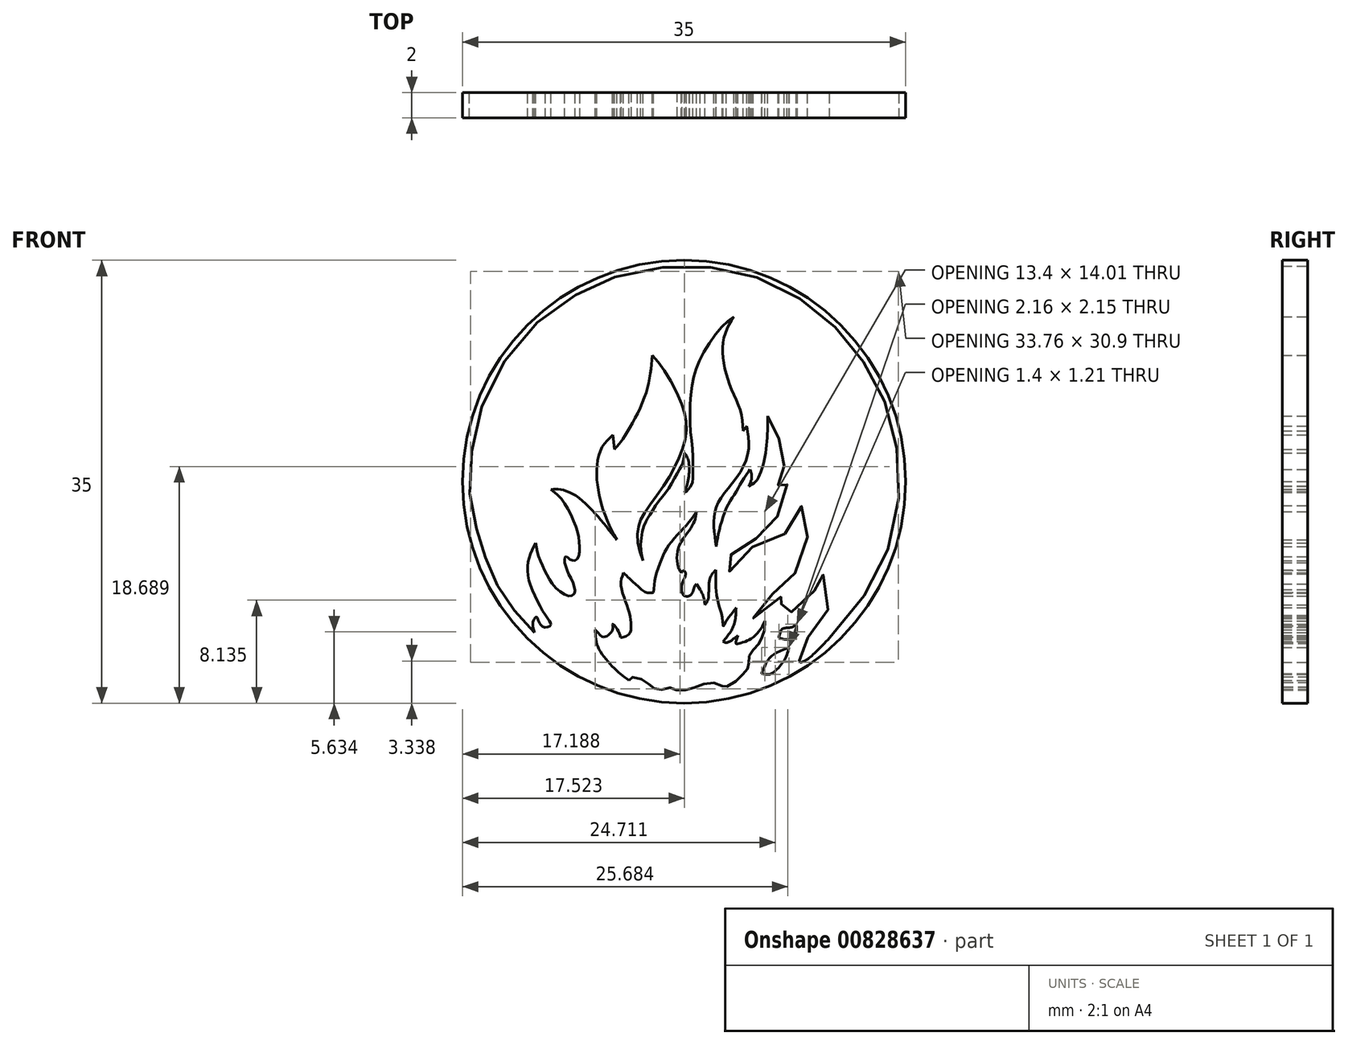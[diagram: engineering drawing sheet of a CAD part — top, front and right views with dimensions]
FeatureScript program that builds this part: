
annotation { "Feature Type Name" : "Feature", "Feature Type Description" : "" }
export const myFeature = defineFeature(function(context is Context, id is Id, definition is map)
    precondition{}
    {
        {
            var Q0;
            Q0=qCreatedBy(makeId("Front.planeOp"),FACE);
            var sketch = newSketch(context, id + "F0", { "sketchPlane" : qUnion([Q0])});
            skCircle(sketch, "E0", {"center": v(0, 0) * mm, "radius": 17.5 * mm});
            skSolve(sketch);
        }
        {
            var Q0;
            Q0=makeQuery(id+"F0.imprint","IMPRINT",FACE,{"disambiguationData":[TD([[makeQuery(id+"F0.imprint","IMPRINT",EDGE,{"derivedFrom":sQuery(id+"F0.wireOp",EDGE,"E0")}),1.0]])]});
            var sketch = newSketch(context, id + "F1", { "sketchPlane" : qUnion([Q0])});
            skFitSpline(sketch, "E1", {"points": [v(-11.8, -11.92) * mm, v(-12.84, -10.88) * mm, v(-13.93, -9.45) * mm, v(-14.73, -8.22) * mm, v(-15.3, -6.9) * mm, v(-16.04, -5.03) * mm, v(-16.38, -3.72) * mm, v(-16.87, -1.59) * mm, v(-16.87, 1.43) * mm, v(-16.3, 4.94) * mm, v(-14.52, 8.98) * mm, v(-11.7, 12.5) * mm, v(-8.56, 14.76) * mm, v(-5.54, 16.14) * mm, v(-1.46, 16.96) * mm, v(2.55, 16.9) * mm, v(6.38, 15.89) * mm, v(9.9, 13.94) * mm, v(12.54, 11.56) * mm, v(14.6, 8.73) * mm, v(16.18, 5.4) * mm, v(16.93, 1.26) * mm, v(16.68, -3.26) * mm, v(14.92, -7.9) * mm, v(11.97, -11.8) * mm, v(9.15, -14.25) * mm, v(9.08, -13.24) * mm, v(10.6, -11.48) * mm, v(11.47, -9.04) * mm, v(10.84, -7.22) * mm, v(10.53, -8.16) * mm, v(9.21, -9.66) * mm, v(7.9, -10.54) * mm, v(7.51, -10.04) * mm, v(8.33, -8.85) * mm, v(6.89, -9.6) * mm, v(5.44, -10.8) * mm, v(6.95, -8.91) * mm, v(8.52, -7.47) * mm, v(9.71, -5.14) * mm, v(9.34, -1.88) * mm, v(8.83, -3.2) * mm, v(6.45, -4.83) * mm, v(4.5, -5.77) * mm, v(3.37, -7.28) * mm, v(3.62, -5.9) * mm, v(5.05, -4.88) * mm, v(6.78, -3.54) * mm, v(7.8, -1.77) * mm, v(8.1, 0) * mm, v(7.85, -0.2) * mm, v(7.45, -0.33) * mm, v(7.63, 0.22) * mm, v(7.89, 1.19) * mm, v(7.8, 2.25) * mm, v(7.04, 4.54) * mm, v(6.6, 5.19) * mm], "startDerivative": vector(-72.23, 66.96) * mm, "endDerivative": vector(-39.78, 46.76) * mm});
            skFitSpline(sketch, "E2", {"points": [v(6.6, 5.19) * mm, v(6.47, 2.59) * mm, v(5.79, 0.19) * mm, v(5.1, -0.37) * mm], "startDerivative": vector(-0.04, -6.43) * mm, "endDerivative": vector(-3.2, -1.68) * mm});
            skFitSpline(sketch, "E3", {"points": [v(5.1, -0.37) * mm, v(5.34, 0.32) * mm, v(5.22, 0.96) * mm], "startDerivative": vector(0.66, 1.34) * mm, "endDerivative": vector(-0.43, 1.32) * mm});
            skFitSpline(sketch, "E4", {"points": [v(5.22, 0.96) * mm, v(4.8, 0.38) * mm, v(4.1, -0.8) * mm, v(3.33, -2.11) * mm, v(2.72, -4.1) * mm, v(2.55, -5.14) * mm], "startDerivative": vector(-2.74, -3.5) * mm, "endDerivative": vector(-0.66, -5.22) * mm});
            skFitSpline(sketch, "E5", {"points": [v(2.55, -5.14) * mm, v(2.36, -3.76) * mm, v(2.42, -2.43) * mm, v(3, -1.12) * mm, v(4.38, 0.67) * mm, v(5.1, 2.68) * mm, v(4.94, 4.4) * mm], "startDerivative": vector(-1.5, 9.13) * mm, "endDerivative": vector(-1.89, 10.06) * mm});
            skFitSpline(sketch, "E6", {"points": [v(4.94, 4.4) * mm, v(4.66, 4) * mm], "startDerivative": vector(-0.29, -0.4) * mm, "endDerivative": vector(-0.29, -0.4) * mm});
            skFitSpline(sketch, "E7", {"points": [v(4.66, 4) * mm, v(4.44, 5.6) * mm, v(3.76, 7.28) * mm, v(3.2, 9) * mm, v(3.03, 10.6) * mm, v(3.34, 11.94) * mm, v(3.94, 13.05) * mm], "startDerivative": vector(-0.6, 9.52) * mm, "endDerivative": vector(4.38, 7.18) * mm});
            skFitSpline(sketch, "E8", {"points": [v(3.94, 13.05) * mm, v(2.79, 12.03) * mm, v(1.39, 9.94) * mm, v(0.77, 8.34) * mm, v(0.5, 6.49) * mm, v(0.47, 4.47) * mm, v(0.64, 2.75) * mm, v(0.7, 1.38) * mm, v(0.7, 0.32) * mm, v(0.6, -0.24) * mm, v(0.19, -0.8) * mm], "startDerivative": vector(-10.97, -8.38) * mm, "endDerivative": vector(-6.85, -7.97) * mm});
            skFitSpline(sketch, "E9", {"points": [v(0.19, -0.8) * mm, v(0.03, -0.85) * mm], "startDerivative": vector(-0.16, -0.06) * mm, "endDerivative": vector(-0.16, -0.06) * mm});
            skFitSpline(sketch, "E10", {"points": [v(0.03, -0.85) * mm, v(0.35, 0.25) * mm, v(0.35, 1.63) * mm, v(0.03, 2.28) * mm], "startDerivative": vector(1.06, 2.97) * mm, "endDerivative": vector(-1.36, 2.03) * mm});
            skFitSpline(sketch, "E11", {"points": [v(0.03, 2.28) * mm, v(-0.09, 1.52) * mm, v(-0.53, 0.69) * mm, v(-1.28, -0.6) * mm, v(-2.04, -1.6) * mm, v(-2.75, -2.69) * mm, v(-3.1, -3.32) * mm, v(-3.43, -4.97) * mm, v(-3.24, -6.23) * mm], "startDerivative": vector(-0.5, -7.58) * mm, "endDerivative": vector(2.2, -8.87) * mm});
            skFitSpline(sketch, "E12", {"points": [v(-3.24, -6.23) * mm, v(-3.66, -4.78) * mm, v(-3.63, -3.66) * mm, v(-3.34, -2.84) * mm, v(-2.48, -1.52) * mm, v(-1.22, 0.31) * mm, v(-0.4, 1.93) * mm, v(0.14, 3.5) * mm, v(0.14, 4.9) * mm, v(-0.25, 6.28) * mm, v(-1.5, 8.71) * mm, v(-2.52, 9.98) * mm], "startDerivative": vector(-6, 16.73) * mm, "endDerivative": vector(-10.81, 11.9) * mm});
            skFitSpline(sketch, "E13", {"points": [v(-2.52, 9.98) * mm, v(-3.09, 6.76) * mm, v(-4.87, 3.35) * mm, v(-5.51, 2.55) * mm], "startDerivative": vector(-0.64, -8.17) * mm, "endDerivative": vector(-2.66, -2.94) * mm});
            skFitSpline(sketch, "E14", {"points": [v(-5.51, 2.55) * mm, v(-5.61, 3.68) * mm], "startDerivative": vector(-0.1, 1.14) * mm, "endDerivative": vector(-0.1, 1.14) * mm});
            skFitSpline(sketch, "E15", {"points": [v(-5.61, 3.68) * mm, v(-6.44, 2.78) * mm, v(-6.88, 1.23) * mm, v(-6.78, -0.6) * mm, v(-6.26, -2.62) * mm, v(-5.32, -4.6) * mm], "startDerivative": vector(-5.48, -4.78) * mm, "endDerivative": vector(4.62, -8.74) * mm});
            skFitSpline(sketch, "E16", {"points": [v(-5.32, -4.6) * mm, v(-6.78, -2.8) * mm, v(-8.52, -1.13) * mm, v(-9.78, -0.6) * mm, v(-10.52, -0.6) * mm], "startDerivative": vector(-4.68, 5.98) * mm, "endDerivative": vector(-4.16, -0.36) * mm});
            skFitSpline(sketch, "E17", {"points": [v(-10.52, -0.6) * mm, v(-9.6, -1.5) * mm, v(-8.58, -3.5) * mm, v(-8.26, -4.97) * mm, v(-8.4, -6.07) * mm, v(-8.78, -6.23) * mm, v(-9.08, -6.1) * mm, v(-9.27, -5.93) * mm, v(-9.4, -5.95) * mm, v(-9.44, -6.4) * mm], "startDerivative": vector(6.3, -4.93) * mm, "endDerivative": vector(0.24, -6.61) * mm});
            skFitSpline(sketch, "E18", {"points": [v(-9.44, -6.4) * mm, v(-9.17, -7.18) * mm, v(-8.69, -8.23) * mm, v(-8.68, -8.83) * mm, v(-9.09, -9.04) * mm, v(-10.21, -8.31) * mm, v(-10.95, -7.12) * mm, v(-11.49, -5.9) * mm, v(-11.73, -4.84) * mm], "startDerivative": vector(1.97, -6.5) * mm, "endDerivative": vector(-1.43, 8) * mm});
            skFitSpline(sketch, "E19", {"points": [v(-11.73, -4.84) * mm, v(-12.2, -5.9) * mm, v(-12.35, -7.26) * mm, v(-11.73, -9.11) * mm, v(-10.78, -10.8) * mm, v(-10.52, -11.2) * mm, v(-10.6, -11.42) * mm, v(-10.96, -11.51) * mm], "startDerivative": vector(-3.32, -6.5) * mm, "endDerivative": vector(-4.63, -0.5) * mm});
            skFitSpline(sketch, "E20", {"points": [v(-10.96, -11.51) * mm, v(-11.15, -11.46) * mm, v(-11.5, -11.02) * mm, v(-11.65, -10.7) * mm, v(-11.86, -10.92) * mm, v(-11.94, -11.4) * mm, v(-11.8, -11.92) * mm], "startDerivative": vector(-1.55, 0.12) * mm, "endDerivative": vector(0.9, -2.65) * mm});
            skFitSpline(sketch, "E21", {"points": [v(-7.01, -11.69) * mm, v(-6.83, -13) * mm, v(-5.61, -14.65) * mm, v(-4.37, -15.7) * mm], "startDerivative": vector(0.01, -4.3) * mm, "endDerivative": vector(3.7, -2.87) * mm});
            skFitSpline(sketch, "E22", {"points": [v(-4.37, -15.7) * mm, v(-4.23, -15.47) * mm, v(-3.51, -15.55) * mm, v(-2.83, -15.98) * mm, v(-2.38, -16.33) * mm, v(-1.83, -16.43) * mm, v(-1.1, -16.27) * mm, v(-0.66, -16.45) * mm, v(0.18, -16.46) * mm, v(1.08, -16.18) * mm, v(2.15, -15.88) * mm, v(2.98, -16.12) * mm, v(3.2, -16.23) * mm, v(3.99, -15.83) * mm, v(4.67, -15.19) * mm, v(5.04, -14.73) * mm, v(5.12, -14.4) * mm, v(5.12, -13.89) * mm, v(5.33, -13.42) * mm, v(5.84, -12.88) * mm, v(6.13, -12.35) * mm, v(6.32, -11.84) * mm, v(6.39, -11) * mm], "startDerivative": vector(2.54, 9.64) * mm, "endDerivative": vector(0.4, 17.25) * mm});
            skFitSpline(sketch, "E23", {"points": [v(6.39, -11) * mm, v(6.05, -11.63) * mm, v(5.25, -12.42) * mm, v(4.4, -12.77) * mm, v(4.09, -12.8) * mm, v(4.24, -12.16) * mm], "startDerivative": vector(-1.37, -3.02) * mm, "endDerivative": vector(1.7, 4.33) * mm});
            skFitSpline(sketch, "E24", {"points": [v(4.24, -12.16) * mm, v(3.36, -12.71) * mm, v(3.1, -12.62) * mm], "startDerivative": vector(-1.53, -1.2) * mm, "endDerivative": vector(-0.68, 0.45) * mm});
            skFitSpline(sketch, "E25", {"points": [v(3.1, -12.62) * mm, v(3.61, -11.95) * mm, v(3.98, -11.16) * mm, v(4.11, -9.94) * mm], "startDerivative": vector(1.76, 2.13) * mm, "endDerivative": vector(0.16, 3.46) * mm});
            skFitSpline(sketch, "E26", {"points": [v(4.11, -9.94) * mm, v(3.68, -10.53) * mm, v(3.26, -11.1) * mm, v(3.1, -11.41) * mm, v(3, -10.65) * mm, v(2.7, -9.57) * mm, v(2.51, -8.4) * mm, v(2.5, -6.98) * mm], "startDerivative": vector(-3.21, -4.6) * mm, "endDerivative": vector(0.15, 7.9) * mm});
            skFitSpline(sketch, "E27", {"points": [v(2.5, -6.98) * mm, v(2.1, -7.51) * mm, v(1.95, -8.55) * mm, v(1.89, -9.32) * mm, v(1.64, -9.73) * mm], "startDerivative": vector(-2, -1.9) * mm, "endDerivative": vector(-1.43, -1.84) * mm});
            skFitSpline(sketch, "E28", {"points": [v(1.64, -9.73) * mm, v(1.55, -9.14) * mm, v(1.27, -8.52) * mm], "startDerivative": vector(-0.1, 1.22) * mm, "endDerivative": vector(-0.64, 1.2) * mm});
            skFitSpline(sketch, "E29", {"points": [v(1.27, -8.52) * mm, v(0.98, -8.08) * mm], "startDerivative": vector(-0.3, 0.44) * mm, "endDerivative": vector(-0.3, 0.44) * mm});
            skFitSpline(sketch, "E30", {"points": [v(0.98, -8.08) * mm, v(0.79, -8.36) * mm, v(0.6, -8.88) * mm, v(0.14, -9.05) * mm, v(-0.15, -8.8) * mm, v(-0.15, -8.08) * mm, v(0.11, -7.35) * mm, v(0.08, -7.11) * mm, v(-0.08, -7.03) * mm, v(-0.23, -7.2) * mm], "startDerivative": vector(-2.14, -2.33) * mm, "endDerivative": vector(-1.73, -2.89) * mm});
            skFitSpline(sketch, "E31", {"points": [v(-0.23, -7.2) * mm, v(-0.52, -6.53) * mm, v(-0.44, -5.22) * mm, v(0.34, -3.94) * mm, v(0.82, -3.11) * mm, v(0.98, -2.36) * mm], "startDerivative": vector(-1.94, 3.6) * mm, "endDerivative": vector(0.61, 4.44) * mm});
            skFitSpline(sketch, "E32", {"points": [v(0.98, -2.36) * mm, v(0.6, -2.94) * mm, v(-0.23, -3.89) * mm, v(-1.2, -5.02) * mm, v(-1.76, -6.09) * mm, v(-2.26, -7.56) * mm, v(-2.4, -8.75) * mm], "startDerivative": vector(-2.68, -4.4) * mm, "endDerivative": vector(-0.4, -6.96) * mm});
            skFitSpline(sketch, "E33", {"points": [v(-2.4, -8.75) * mm, v(-2.99, -8.75) * mm, v(-3.72, -8.2) * mm, v(-4.8, -7.2) * mm], "startDerivative": vector(-2.24, -0.36) * mm, "endDerivative": vector(-2.69, 2.5) * mm});
            skFitSpline(sketch, "E34", {"points": [v(-4.8, -7.2) * mm, v(-5, -8.08) * mm, v(-4.62, -9.46) * mm, v(-4.24, -10.77) * mm, v(-4.2, -11.42) * mm, v(-4.28, -11.96) * mm, v(-4.8, -12.28) * mm, v(-5.01, -12.3) * mm], "startDerivative": vector(-2.05, -5.34) * mm, "endDerivative": vector(-2.47, 0.07) * mm});
            skFitSpline(sketch, "E35", {"points": [v(-7.01, -11.69) * mm, v(-6.6, -12.16) * mm, v(-6.35, -12.27) * mm, v(-5.91, -12.06) * mm, v(-5.63, -11.6) * mm, v(-5.65, -11.25) * mm, v(-5.27, -11.69) * mm, v(-5.01, -12.3) * mm], "startDerivative": vector(2.65, -3.36) * mm, "endDerivative": vector(1.03, -3.51) * mm});
            skFitSpline(sketch, "E36", {"points": [v(8.85, -11.26) * mm, v(8.86, -11.9) * mm, v(8.36, -12.44) * mm, v(7.48, -12.35) * mm], "startDerivative": vector(0.36, -2.09) * mm, "endDerivative": vector(-2.57, 0.74) * mm});
            skFitSpline(sketch, "E37", {"points": [v(8.85, -11.26) * mm, v(8.43, -11.51) * mm, v(7.78, -11.63) * mm, v(7.48, -12.35) * mm], "startDerivative": vector(-1.24, -1.09) * mm, "endDerivative": vector(-0.46, -2.44) * mm});
            skFitSpline(sketch, "E38", {"points": [v(8.3, -13.09) * mm, v(7.06, -13.66) * mm, v(6.49, -14.33) * mm, v(6.13, -15.15) * mm, v(6.13, -15.16) * mm], "startDerivative": vector(-3.71, -1.47) * mm, "endDerivative": vector(0.05, -0.15) * mm});
            skFitSpline(sketch, "E39", {"points": [v(8.3, -13.09) * mm, v(7.98, -13.98) * mm, v(7.41, -14.73) * mm, v(6.77, -15.22) * mm, v(6.13, -15.16) * mm], "startDerivative": vector(-0.91, -3.45) * mm, "endDerivative": vector(-2.95, 0.76) * mm});
            skFitSpline(sketch, "E40", {"points": [v(9.08, -14.21) * mm, v(11.48, -12.35) * mm], "startDerivative": vector(2.4, 1.87) * mm, "endDerivative": vector(2.4, 1.87) * mm});
            skFitSpline(sketch, "E41", {"points": [v(-0.23, -7.2) * mm, v(-0.15, -8.08) * mm], "startDerivative": vector(0.08, -0.88) * mm, "endDerivative": vector(0.08, -0.88) * mm});
            skSolve(sketch);
        }
        {
            var Q0;
            {var subQ1=sQuery(id+"F1.wireOp",EDGE,"E2");Q0=makeQuery(id+"F1.imprint","IMPRINT",FACE,{"disambiguationData":[TD([[makeQuery(id+"F1.imprint","IMPRINT",EDGE,{"derivedFrom":subQ1}),1.0]])]});}
            extrude(context, id + "F2", {"entities" : qUnion([Q0]), "depth" : 2 * mm, "offsetDistance" : 25 * mm});
        }
    });
